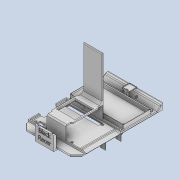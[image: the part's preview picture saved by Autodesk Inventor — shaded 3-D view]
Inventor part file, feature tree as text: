
AUTODESK INVENTOR PART (.ipt)
format: ipt  version: 2020 (Build 240168000, 168)  size: 1,716,736 bytes
history: native  units: mm
features: extrude x45, sketch x44, fillet x33, chamfer x13, other x1
ambient origin geometry x8: Origin, YZ Plane, XZ Plane, XY Plane, X Axis, Y Axis, Z Axis, Center Point
bodies: Body1 (feature_tree)
feature tree (136):
  other  "Твердое тело1"
  sketch  "Эскиз1"
  extrude  "Выдавливание1"  Depth=30.0mm
  extrude  "Выдавливание2"  Depth=145.0mm
  extrude  "Выдавливание3"  Depth=2.8mm
  chamfer  "Фаска1"  Distance=2.8mm
  sketch  "Эскиз3"
  extrude  "Выдавливание4"  Depth=22.0mm
  extrude  "Выдавливание5"  Depth=2.0mm
  extrude  "Выдавливание6"  Depth=4.0mm
  chamfer  "Фаска2"  Distance=4.0mm
  extrude  "Выдавливание7"  Depth=2.8mm
  extrude  "Выдавливание8"  Depth=2.8mm
  fillet  "Сопряжение1"  Radius=135.0mm
  fillet  "Сопряжение2"  Radius=135.0mm
  fillet  "Сопряжение3"  Radius=2.5mm
  chamfer  "Фаска3"  Distance=10.0mm
  chamfer  "Фаска4"  Distance=2.5mm
  fillet  "Сопряжение4"  Radius=20.0mm
  fillet  "Сопряжение5"  Radius=2.0mm
  sketch  "Эскиз11"
  extrude  "Выдавливание9"  Depth=30.0mm TaperAngle=0.0deg
  extrude  "Выдавливание10"  Depth=30.0mm TaperAngle=0.0deg
  extrude  "Выдавливание11"  Depth=10.0mm
  fillet  "Сопряжение6"  Radius=7.0mm
  fillet  "Сопряжение7"  Radius=2.0mm
  extrude  "Выдавливание12"  Depth=41.0mm
  extrude  "Выдавливание13"  Depth=83.0mm
  extrude  "Выдавливание14"  Depth=3.5mm
  fillet  "Сопряжение11"  Radius=10.0mm
  fillet  "Сопряжение12"  Radius=1.5mm
  chamfer  "Фаска5"  Distance=1.5mm
  fillet  "Сопряжение14"  Radius=1.5mm
  chamfer  "Фаска6"  Distance=1.5mm
  chamfer  "Фаска7"  Distance=7.0mm
  chamfer  "Фаска8"  Distance=5.5mm
  chamfer  "Фаска9"  Distance=7.0mm
  chamfer  "Фаска10"  Distance=1.0mm
  fillet  "Сопряжение15"  Radius=1.0mm
  extrude  "Выдавливание15"  Depth=1.0mm
  fillet  "Сопряжение17"  Radius=10.0mm
  extrude  "Выдавливание16"  Depth=1.0mm TaperAngle=45.0deg
  extrude  "Выдавливание17"  Depth=1.0mm
  fillet  "Сопряжение18"  Radius=1.0mm
  extrude  "Выдавливание20"  Depth=87.0mm
  fillet  "Сопряжение19"  Radius=58.0mm
  extrude  "Выдавливание22"  Depth=15.0mm
  fillet  "Сопряжение21"  Radius=1.5mm
  fillet  "Сопряжение22"  Radius=1.5mm
  chamfer  "Фаска12"  Distance=2.7mm
  extrude  "Выдавливание23"  Depth=4.5mm
  chamfer  "Фаска13"  Distance=4.5mm
  chamfer  "Фаска14"  Distance=2.7mm
  extrude  "Выдавливание24"  Depth=4.5mm
  fillet  "Сопряжение23"  Radius=4.5mm
  extrude  "Выдавливание25"  Depth=2.7mm
  extrude  "Выдавливание26"  Depth=58.0mm
  fillet  "Сопряжение24"  Radius=2.7mm
  extrude  "Выдавливание27"  Depth=3.0mm TaperAngle=0.0deg
  extrude  "Выдавливание28"  Depth=3.0mm TaperAngle=0.0deg
  extrude  "Выдавливание29"  TaperAngle=0.0deg  [1 undecoded]
  fillet  "Сопряжение25"  Radius=10.0mm
  extrude  "Выдавливание30"  Depth=1.0mm TaperAngle=0.0deg
  fillet  "Сопряжение26"  Radius=2.0mm
  extrude  "Выдавливание31"  Depth=1.0mm
  fillet  "Сопряжение27"  Radius=30.0mm
  extrude  "Выдавливание32"  Depth=30.0mm
  fillet  "Сопряжение28"  Radius=30.0mm
  fillet  "Сопряжение29"  Radius=30.0mm
  extrude  "Выдавливание33"  Depth=20.0mm TaperAngle=0.0deg
  extrude  "Выдавливание34"  Depth=2.0mm TaperAngle=0.0deg
  extrude  "Выдавливание35"  Depth=5.0mm
  extrude  "Выдавливание36"  Depth=3.5mm
  extrude  "Выдавливание37"  Depth=3.5mm
  fillet  "Сопряжение30"  Radius=25.0mm
  fillet  "Сопряжение31"  Radius=0.5mm
  extrude  "Выдавливание38"  Depth=0.5mm
  extrude  "Выдавливание39"  Depth=2.0mm TaperAngle=45.0deg
  extrude  "Выдавливание40"  Depth=3.0mm
  extrude  "Выдавливание41"  Depth=2.0mm TaperAngle=45.0deg
  fillet  "Сопряжение32"  Radius=1.0mm
  fillet  "Сопряжение33"  Radius=1.0mm
  extrude  "Выдавливание42"  Depth=2.0mm TaperAngle=45.0deg
  extrude  "Выдавливание44"  Depth=1.0mm TaperAngle=45.0deg
  extrude  "Выдавливание45"  Depth=2.0mm
  extrude  "Выдавливание46"  TaperAngle=0.0deg  [1 undecoded]
  extrude  "Выдавливание47"  Depth=0.5mm
  extrude  "Выдавливание48"  Depth=1.0mm TaperAngle=0.0deg
  fillet  "Сопряжение34"  Radius=10.0mm
  fillet  "Сопряжение35"  Radius=0.5mm
  fillet  "Сопряжение36"  Radius=8.0mm
  fillet  "Сопряжение37"  Radius=6.0mm
  fillet  "Сопряжение38"  Radius=10.0mm
  extrude  "Выдавливание49"  Depth=0.5mm
  fillet  "Сопряжение39"  Radius=10.0mm
  sketch  "Эскиз2"
  sketch  "Эскиз4"
  sketch  "Эскиз5"
  sketch  "Эскиз6"
  sketch  "Эскиз7"
  sketch  "Эскиз10"
  sketch  "Эскиз12"
  sketch  "Эскиз13"
  sketch  "Эскиз14"
  sketch  "Эскиз15"
  sketch  "Эскиз16"
  sketch  "Эскиз17"
  sketch  "Эскиз18"
  sketch  "Эскиз21"
  sketch  "Эскиз23"
  sketch  "Эскиз24"
  sketch  "Эскиз25"
  sketch  "Эскиз26"
  sketch  "Эскиз27"
  sketch  "Эскиз28"
  sketch  "Эскиз29"
  sketch  "Эскиз30"
  sketch  "Эскиз31"
  sketch  "Эскиз32"
  sketch  "Эскиз33"
  sketch  "Эскиз34"
  sketch  "Эскиз35"
  sketch  "Эскиз36"
  sketch  "Эскиз37"
  sketch  "Эскиз38"
  sketch  "Эскиз39"
  sketch  "Эскиз40"
  sketch  "Эскиз41"
  sketch  "Эскиз42"
  sketch  "Эскиз43"
  sketch  "Эскиз45"
  sketch  "Эскиз46"
  sketch  "Эскиз47"
  sketch  "Эскиз48"
  sketch  "Эскиз49"
  sketch  "Эскиз50"
note: 2 required parameter values undecoded (feature->parameter linkage not recoverable at this tier; creation-order binding heuristic only, values carry confidence <= 0.55)
